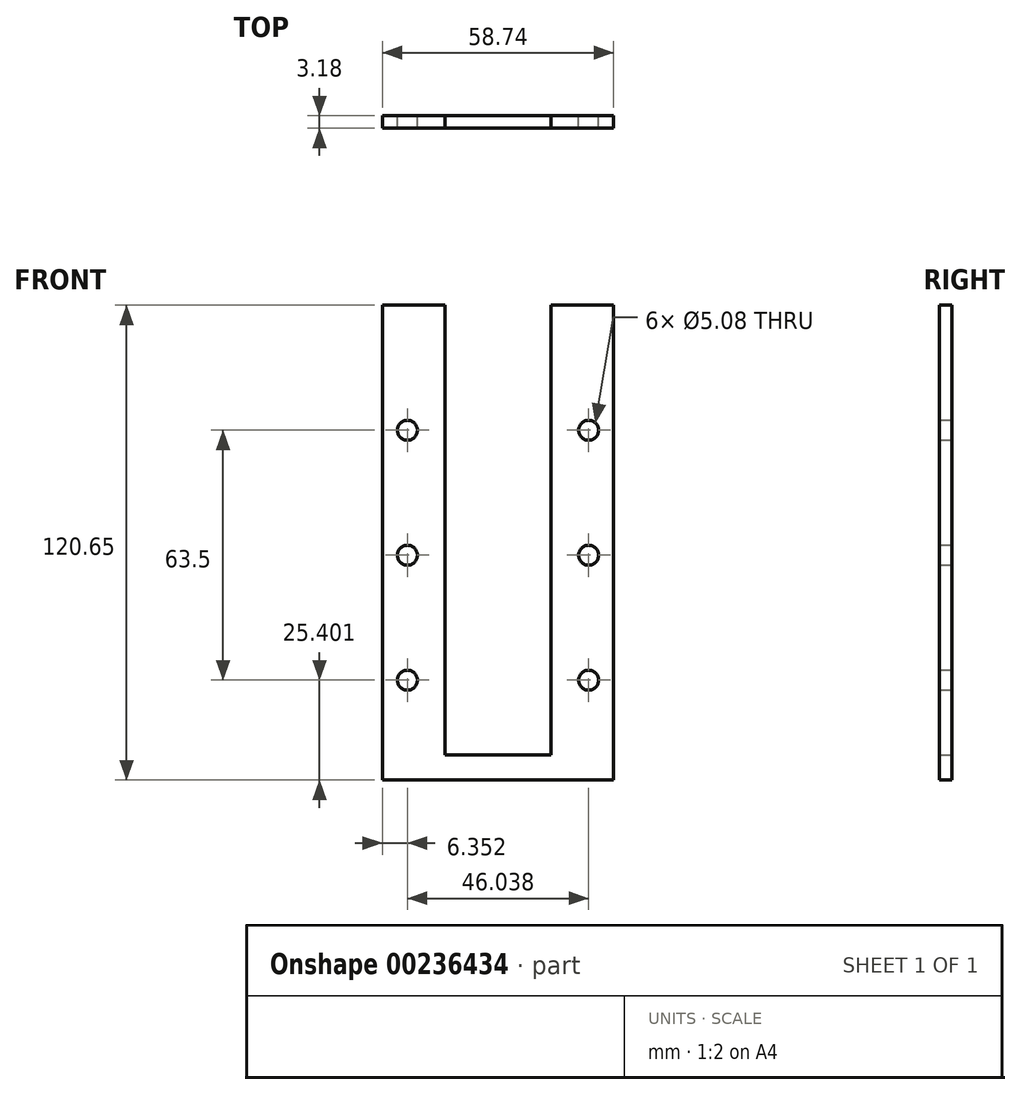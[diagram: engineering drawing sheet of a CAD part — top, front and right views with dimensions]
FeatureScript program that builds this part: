
annotation { "Feature Type Name" : "Feature", "Feature Type Description" : "" }
export const myFeature = defineFeature(function(context is Context, id is Id, definition is map)
    precondition{}
    {
        {
            var Q0;
            Q0=qCreatedBy(makeId("Front.planeOp"),FACE);
            var sketch = newSketch(context, id + "F0", { "sketchPlane" : qUnion([Q0])});
            skLineSegment(sketch, "E0", {"start": v(-48.68, 9.24) * mm, "end": v(-48.68, -105.06) * mm});
            skLineSegment(sketch, "E1", {"start": v(-5.82, -111.4) * mm, "end": v(-64.56, -111.4) * mm});
            skLineSegment(sketch, "E2", {"start": v(-64.56, -111.4) * mm, "end": v(-64.56, 9.24) * mm});
            skLineSegment(sketch, "E3", {"start": v(-64.56, 9.24) * mm, "end": v(-51.86, 9.24) * mm});
            skLineSegment(sketch, "E4", {"start": v(-51.86, 9.24) * mm, "end": v(-48.68, 9.24) * mm});
            skLineSegment(sketch, "E5", {"start": v(-48.68, -105.06) * mm, "end": v(-51.86, -105.06) * mm});
            skLineSegment(sketch, "E6", {"start": v(-51.86, -105.06) * mm, "end": v(-51.86, 9.24) * mm});
            skCircle(sketch, "E7", {"center": v(-58.2, -22.5) * mm, "radius": 2.54 * mm});
            skCircle(sketch, "E8", {"center": v(-58.2, -54.26) * mm, "radius": 2.54 * mm});
            skCircle(sketch, "E9", {"center": v(-58.2, -86) * mm, "radius": 2.54 * mm});
            skCircle(sketch, "E10", {"center": v(-12.17, -22.5) * mm, "radius": 2.54 * mm});
            skCircle(sketch, "E11", {"center": v(-12.17, -54.26) * mm, "radius": 2.54 * mm});
            skCircle(sketch, "E12", {"center": v(-12.17, -86) * mm, "radius": 2.54 * mm});
            skLineSegment(sketch, "E13", {"start": v(-48.68, -105.06) * mm, "end": v(-21.7, -105.06) * mm});
            skLineSegment(sketch, "E14", {"start": v(-21.7, -105.06) * mm, "end": v(-18.52, -105.06) * mm});
            skLineSegment(sketch, "E15", {"start": v(-5.82, -111.4) * mm, "end": v(-5.82, 9.24) * mm});
            skLineSegment(sketch, "E16", {"start": v(-5.82, 9.24) * mm, "end": v(-18.52, 9.24) * mm});
            skLineSegment(sketch, "E17", {"start": v(-18.52, 9.24) * mm, "end": v(-18.52, -105.06) * mm});
            skLineSegment(sketch, "E18", {"start": v(-18.52, 9.24) * mm, "end": v(-21.7, 9.24) * mm});
            skLineSegment(sketch, "E19", {"start": v(-21.7, 9.24) * mm, "end": v(-21.7, -105.06) * mm});
            skSolve(sketch);
        }
        {
            var Q0;
            Q0=makeQuery(id+"F0.imprint","IMPRINT",FACE,{"disambiguationData":[TD([[makeQuery(id+"F0.imprint","IMPRINT",EDGE,{"derivedFrom":sQuery(id+"F0.wireOp",EDGE,"E0")}),-1.0]])]});
            var Q1;
            Q1=makeQuery(id+"F0.imprint","IMPRINT",FACE,{"disambiguationData":[TD([[makeQuery(id+"F0.imprint","IMPRINT",EDGE,{"derivedFrom":sQuery(id+"F0.wireOp",EDGE,"E1")}),-1.0]])]});
            var Q2;
            Q2=makeQuery(id+"F0.imprint","IMPRINT",FACE,{"disambiguationData":[TD([[makeQuery(id+"F0.imprint","IMPRINT",EDGE,{"derivedFrom":sQuery(id+"F0.wireOp",EDGE,"E14")}),1.0]])]});
            extrude(context, id + "F1", {"entities" : qUnion([Q0, Q1, Q2]), "depth" : 3.17 * mm});
        }
    });
